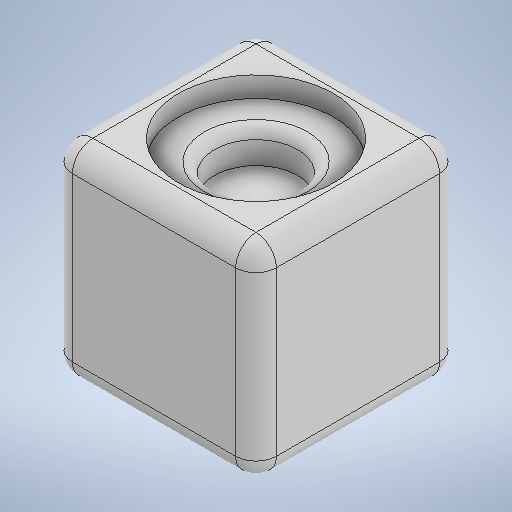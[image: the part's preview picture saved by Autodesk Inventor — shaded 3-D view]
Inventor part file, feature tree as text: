
AUTODESK INVENTOR PART (.ipt)
format: ipt  version: 2025 (Build 290162000, 162)  size: 306,176 bytes
history: native  units: in
note: dims shown in document units (in); Inventor stores cm internally (conversion verified against a paired STEP export)
features: extrude x7, sketch x7, fillet x5
ambient origin geometry x8: Origin, YZ Plane, XZ Plane, XY Plane, X Axis, Y Axis, Z Axis, Center Point
bodies: Solid1 (feature_tree)
feature tree (19):
  extrude  "Extrusion1"  Depth=0.7874in
  extrude  "Extrusion2"  Depth=0.7874in
  extrude  "Extrusion3"  Depth=0.3937in
  extrude  "Extrusion4"  Depth=0.0787in
  fillet  "Fillet1"  Radius=0.0787in
  extrude  "Extrusion5"  Depth=0.3937in
  extrude  "Extrusion6"  Depth=0.0787in TaperAngle=0.0deg
  extrude  "Extrusion7"  Depth=0.0394in
  fillet  "Fillet2"  Radius=0.126in
  fillet  "Fillet3"  Radius=0.3134in
  fillet  "Fillet4"  Radius=0.126in
  fillet  "Fillet5"  Radius=0.3205in
  sketch  "Sketch1"  dims[d0=0.7874in d1=0.7874in]
  sketch  "Sketch2"  dims[d2=0.7874in d3=0.0in d4=0.5984in]
  sketch  "Sketch3"  dims[d5=0.3937in d6=0.3937in]
  sketch  "Sketch4"  dims[d7=0.0787in d8=0.0in d9=0.5984in d10=0.0787in d11=0.0in]
  sketch  "Sketch5"  dims[d12=0.5984in d13=0.3937in]
  sketch  "Sketch6"  dims[d14=0.3937in d15=0.0787in d16=0.0in]
  sketch  "Sketch7"  dims[d17=0.0787in d18=0.3205in d19=0.126in d20=0.0in d21=0.3134in d22=0.126in d23=0.0in d24=0.3205in d25=0.126in d26=0.0in d27=0.0787in d28=0.0394in d29=0.0394in d30=0.0394in]
